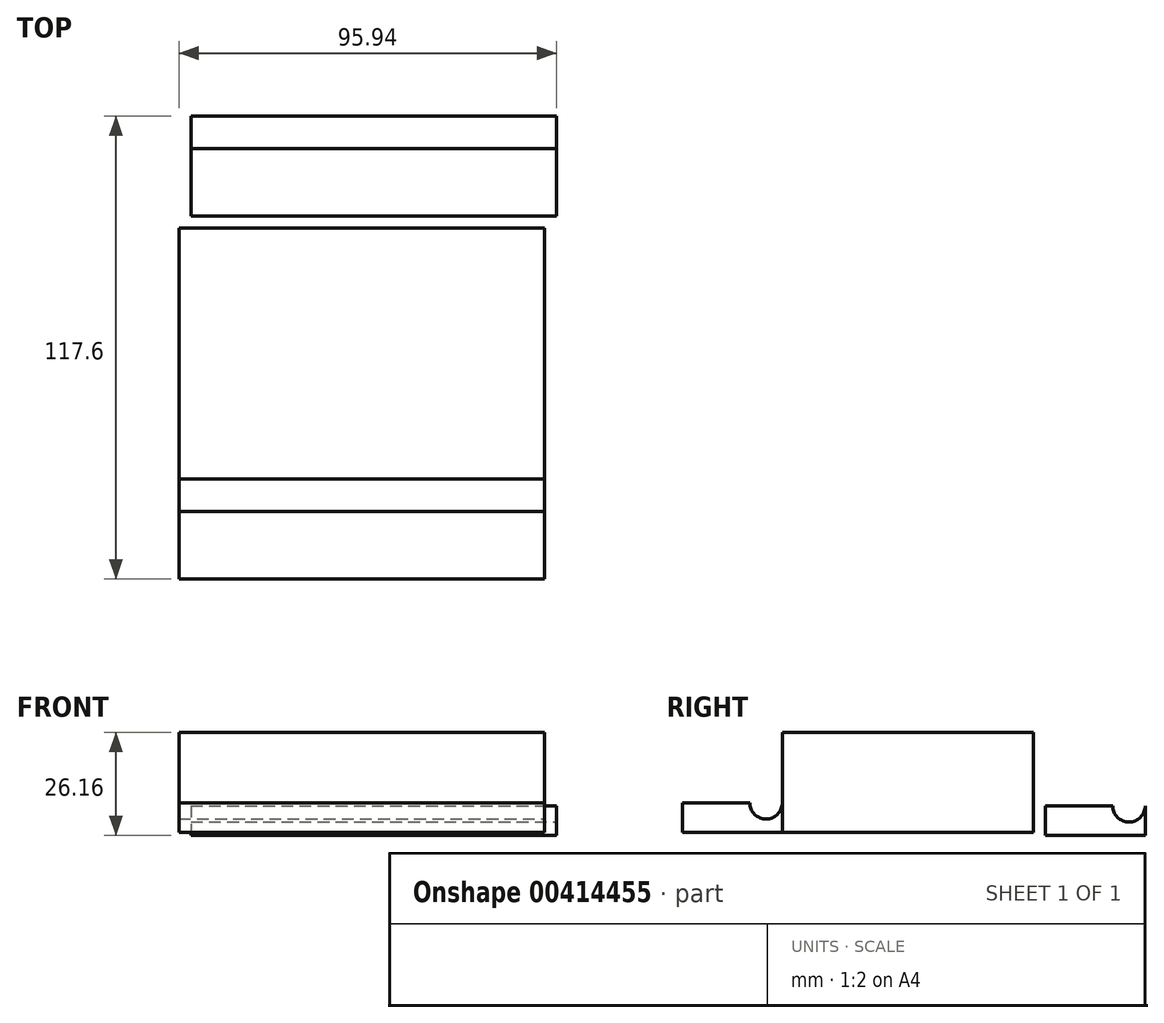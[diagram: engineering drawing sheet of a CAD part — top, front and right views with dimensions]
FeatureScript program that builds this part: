
annotation { "Feature Type Name" : "Feature", "Feature Type Description" : "" }
export const myFeature = defineFeature(function(context is Context, id is Id, definition is map)
    precondition{}
    {
        {
            var Q0;
            Q0=qCreatedBy(makeId("Top.planeOp"),FACE);
            var sketch = newSketch(context, id + "F0", { "sketchPlane" : qUnion([Q0])});
            skLineSegment(sketch, "E0.bottom", {"start": v(0, 0) * mm, "end": v(-92.9, 0) * mm});
            skLineSegment(sketch, "E0.top", {"start": v(0, -63.8) * mm, "end": v(-92.9, -63.8) * mm});
            skLineSegment(sketch, "E0.left", {"start": v(0, 0) * mm, "end": v(0, -63.8) * mm});
            skLineSegment(sketch, "E0.right", {"start": v(-92.9, 0) * mm, "end": v(-92.9, -63.8) * mm});
            skSolve(sketch);
        }
        {
            var Q0;
            Q0=makeQuery(id+"F0.imprint","IMPRINT",FACE,{"disambiguationData":[TD([[makeQuery(id+"F0.imprint","IMPRINT",EDGE,{"derivedFrom":sQuery(id+"F0.wireOp",EDGE,"E0.bottom")}),1.0]])]});
            extrude(context, id + "F1", {"entities" : qUnion([Q0]), "depth" : 25.4 * mm});
        }
        {
            var Q0;
            Q0=makeQuery(id+"F1.opExtrude","SWEPT_FACE",FACE,{"disambiguationData":[OSD([sQuery(id+"F0.wireOp",EDGE,"E0.top")])]});
            var sketch = newSketch(context, id + "F2", { "sketchPlane" : qUnion([Q0])});
            skLineSegment(sketch, "E1.bottom", {"start": v(-92.9, 0) * mm, "end": v(0, 0) * mm});
            skLineSegment(sketch, "E1.top", {"start": v(-92.9, 7.57) * mm, "end": v(0, 7.57) * mm});
            skLineSegment(sketch, "E1.left", {"start": v(-92.9, 0) * mm, "end": v(-92.9, 7.57) * mm});
            skLineSegment(sketch, "E1.right", {"start": v(0, 0) * mm, "end": v(0, 7.57) * mm});
            skSolve(sketch);
        }
        {
            var Q0;
            Q0=makeQuery(id+"F2.imprint","IMPRINT",FACE,{"disambiguationData":[TD([[makeQuery(id+"F2.imprint","IMPRINT",EDGE,{"derivedFrom":sQuery(id+"F2.wireOp",EDGE,"E1.bottom")}),-1.0]])]});
            extrude(context, id + "F3", {"entities" : qUnion([Q0]), "depth" : 25.4 * mm});
        }
        {
            var Q0;
            Q0=makeQuery(id+"F3.opExtrude","SWEPT_FACE",FACE,{"disambiguationData":[OSD([sQuery(id+"F2.wireOp",EDGE,"E1.right")])]});
            var sketch = newSketch(context, id + "F4", { "sketchPlane" : qUnion([Q0])});
            skArc(sketch, "E2", {"start": v(-72.1, 7.57) * mm, "mid": v(-67.95, 3.42) * mm, "end": v(-63.8, 7.57) * mm});
            skSolve(sketch);
        }
        {
            var Q0;
            {var subQ0=sQuery(id+"F4.wireOp",EDGE,"E2");Q0=makeQuery(id+"F4.imprint","IMPRINT",FACE,{"disambiguationData":[TD([[makeQuery(id+"F4.imprint","IMPRINT",EDGE,{"derivedFrom":subQ0}),1.0]])]});}
            extrude(context, id + "F5", {"entities" : qUnion([Q0]), "operationType" : NewBodyOperationType.REMOVE, "oppositeDirection" : true, "depth" : 155.2 * mm});
        }
        {
            var Q0;
            Q0=makeQuery(id+"F3.opExtrude","SWEPT_BODY",BODY,{"disambiguationData":[OSD([sQuery(id+"F2.wireOp",EDGE,"E1.bottom"),sQuery(id+"F2.wireOp",EDGE,"E1.top"),sQuery(id+"F2.wireOp",EDGE,"E1.left"),sQuery(id+"F2.wireOp",EDGE,"E1.right")])]});
            transform(context, id + "F6", {"entities" : qUnion([Q0]), "transformType" : TransformType.TRANSLATION_3D, "dx" : 3.05 * mm, "dy" : 92.2 * mm, "dz" : -0.76 * mm, "makeCopy" : true});
        }
    });
